# Revit family: TESK_Насос вертикальный_SVM(T)-120
name_source: partatom
category: Оборудование
units: mm (PartAtom-declared; Revit-internal decimal feet)

## family parameters
Всегда вертикально = Да
Классификация = Насос
На основе рабочей плоскости = Нет
Общий = Нет
При загрузке вырезать с полостями = Нет
Размер круглого соединителя = Использовать диаметр
Тип детали = Вставляется
Точка расчета площади = Нет

## types (38) — shared parameters
ADSK_Версия Revit = 2019
ADSK_Версия семейства = 1.0
ADSK_Диаметр условный = 125 мм
ADSK_Единица измерения = шт.
ADSK_Завод-изготовитель = TESK
ADSK_Классификация нагрузок = Прочее
ADSK_Количество = 1
ADSK_Количество фаз = 3
ADSK_Количество фаз числовое = 3
ADSK_Коэффициент мощности = 1
ADSK_Наименование краткое = Вертикальный многоступенчатый центробежный насос
ADSK_Напряжение = 400 В
URL = www.teskpump.ru
Материал_1 = TESK_Черный_Условный
Материал_2 = TESK_Нержавеющая сталь
Материал_КорпусДвигателя = TESK_Черный_Ребра_Условный
Таблица_Поиска = TESK_SVM(T)-120
УГО_Длина = 380 мм
Фланец_Толщина = 30 мм

## per-type parameters (varying)
| type | ADSK_Код изделия | ADSK_Масса | ADSK_Масса_Текст | ADSK_Наименование | ADSK_Номинальная мощность | ADSK_Полная мощность | D_Башня | Высота_Башня | Высота_Корпуса | Двигатель_Высота | Двигатель_ОтступКоробки | Двигатель_Ширина | Материал_КорпусУлитка | Напор максимальный | Толщина_ФланцаДвигателя |
| SVM 120-1 11kW 3x380V 50Hz IE3 | 77120-100003380NSSF | 230 | 230 | Вертикальный многоступенчатый центробежный насос SVM, DN125, PN25-40, Hmax=22м (3x380V 50Hz IE3) | 11 кВт | 11 кВ·А | 263 мм | 300 мм | 840 мм | 580 мм | 260 мм | 350 мм | TESK_Нержавеющая сталь | 22 | 17 мм |
| SVM 120-2-2 15kW 3x380V 50Hz IE3 | 77120-20-20003380NSSF | 245 | 245 | Вертикальный многоступенчатый центробежный насос SVM, DN125, PN25-40, Hmax=34м (3x380V 50Hz IE3) | 15 кВт | 15 кВ·А | 263 мм | 340 мм | 1000 мм | 580 мм | 260 мм | 350 мм | TESK_Нержавеющая сталь | 34 | 17 мм |
| SVM 120-2-1 18.5kW 3x380V 50Hz IE3 | 77120-20-10003380NSSF | 250 | 250 | Вертикальный многоступенчатый центробежный насос SVM, DN125, PN25-40, Hmax=41м (3x380V 50Hz IE3) | 19 кВт | 19 кВ·А | 263 мм | 340 мм | 1000 мм | 610 мм | 260 мм | 350 мм | TESK_Нержавеющая сталь | 41 | 18 мм |
| SVM 120-2 22kW 3x380V 50Hz IE3 | 77120-200003380NSSF | 285 | 285 | Вертикальный многоступенчатый центробежный насос SVM, DN125, PN25-40, Hmax=46м (3x380V 50Hz IE3) | 22 кВт | 22 кВ·А | 270 мм | 340 мм | 1000 мм | 645 мм | 285 мм | 360 мм | TESK_Нержавеющая сталь | 46 | 19 мм |
| SVM 120-3-2 30kW 3x380V 50Hz IE3 | 77120-30-20003380NSSF | 358 | 358 | Вертикальный многоступенчатый центробежный насос SVM, DN125, PN25-40, Hmax=57м (3x380V 50Hz IE3) | 30 кВт | 30 кВ·А | 300 мм | 380 мм | 1160 мм | 705 мм | 310 мм | 400 мм | TESK_Нержавеющая сталь | 57 | 21 мм |
| SVM 120-3-1 30kW 3x380V 50Hz IE3 | 77120-30-10003380NSSF | 360 | 360 | Вертикальный многоступенчатый центробежный насос SVM, DN125, PN25-40, Hmax=64м (3x380V 50Hz IE3) | 30 кВт | 30 кВ·А | 300 мм | 380 мм | 1160 мм | 705 мм | 310 мм | 400 мм | TESK_Нержавеющая сталь | 64 | 21 мм |
| SVM 120-3 30kW 3x380V 50Hz IE3 | 77120-300003380NSSF | 360 | 360 | Вертикальный многоступенчатый центробежный насос SVM, DN125, PN25-40, Hmax=69.5м (3x380V 50Hz IE3) | 30 кВт | 30 кВ·А | 300 мм | 380 мм | 1160 мм | 705 мм | 310 мм | 400 мм | TESK_Нержавеющая сталь | 69.5 | 21 мм |
| SVM 120-4-2 37kW 3x380V 50Hz IE3 | 77120-40-20003380NSSF | 400 | 400 | Вертикальный многоступенчатый центробежный насос SVM, DN125, PN25-40, Hmax=80.5м (3x380V 50Hz IE3) | 37 кВт | 37 кВ·А | 300 мм | 420 мм | 1320 мм | 705 мм | 310 мм | 400 мм | TESK_Нержавеющая сталь | 80.5 | 21 мм |
| SVM 120-4-1 37kW 3x380V 50Hz IE3 | 77120-40-10003380NSSF | 400 | 400 | Вертикальный многоступенчатый центробежный насос SVM, DN125, PN25-40, Hmax=87м (3x380V 50Hz IE3) | 37 кВт | 37 кВ·А | 300 мм | 420 мм | 1320 мм | 705 мм | 310 мм | 400 мм | TESK_Нержавеющая сталь | 87 | 21 мм |
| SVM 120-4 45kW 3x380V 50Hz IE3 | 77120-400003380NSSF | 460 | 460 | Вертикальный многоступенчатый центробежный насос SVM, DN125, PN25-40, Hmax=92.5м (3x380V 50Hz IE3) | 45 кВт | 45 кВ·А | 345 мм | 420 мм | 1320 мм | 740 мм | 340 мм | 460 мм | TESK_Нержавеющая сталь | 92.5 | 22 мм |
| SVM 120-5-2 45kW 3x380V 50Hz IE3 | 77120-50-20003380NSSF | 470 | 470 | Вертикальный многоступенчатый центробежный насос SVM, DN125, PN25-40, Hmax=104.5м (3x380V 50Hz IE3) | 45 кВт | 45 кВ·А | 345 мм | 480 мм | 1480 мм | 740 мм | 340 мм | 460 мм | TESK_Нержавеющая сталь | 104.5 | 22 мм |
| SVM 120-5-1 45kW 3x380V 50Hz IE3 | 77120-50-10003380NSSF | 470 | 470 | Вертикальный многоступенчатый центробежный насос SVM, DN125, PN25-40, Hmax=110.5м (3x380V 50Hz IE3) | 45 кВт | 45 кВ·А | 345 мм | 480 мм | 1480 мм | 740 мм | 340 мм | 460 мм | TESK_Нержавеющая сталь | 110.5 | 22 мм |
| SVM 120-5 55kW 3x380V 50Hz IE3 | 77120-500003380NSSF | 575 | 575 | Вертикальный многоступенчатый центробежный насос SVM, DN125, PN25-40, Hmax=115.5м (3x380V 50Hz IE3) | 55 кВт | 55 кВ·А | 413 мм | 500 мм | 1510 мм | 810 мм | 370 мм | 550 мм | TESK_Нержавеющая сталь | 115.5 | 24 мм |
| SVM 120-6-2 55kW 3x380V 50Hz IE3 | 77120-60-20003380NSSF | 585 | 585 | Вертикальный многоступенчатый центробежный насос SVM, DN125, PN25-40, Hmax=128м (3x380V 50Hz IE3) | 55 кВт | 55 кВ·А | 413 мм | 560 мм | 1670 мм | 810 мм | 370 мм | 550 мм | TESK_Нержавеющая сталь | 128 | 24 мм |
| SVM 120-6-1 55kW 3x380V 50Hz IE3 | 77120-60-10003380NSSF | 585 | 585 | Вертикальный многоступенчатый центробежный насос SVM, DN125, PN25-40, Hmax=134м (3x380V 50Hz IE3) | 55 кВт | 55 кВ·А | 413 мм | 560 мм | 1670 мм | 810 мм | 370 мм | 550 мм | TESK_Нержавеющая сталь | 134 | 24 мм |
| SVM 120-6 75kW 3x380V 50Hz IE3 | 77120-600003380NSSF | 705 | 705 | Вертикальный многоступенчатый центробежный насос SVM, DN125, PN25-40, Hmax=139м (3x380V 50Hz IE3) | 75 кВт | 75 кВ·А | 435 мм | 560 мм | 1670 мм | 870 мм | 410 мм | 580 мм | TESK_Нержавеющая сталь | 139 | 26 мм |
| SVM 120-7-2 75kW 3x380V 50Hz IE3 | 77120-70-20003380NSSF | 713 | 713 | Вертикальный многоступенчатый центробежный насос SVM, DN125, PN25-40, Hmax=151м (3x380V 50Hz IE3) | 75 кВт | 75 кВ·А | 435 мм | 600 мм | 1830 мм | 870 мм | 410 мм | 580 мм | TESK_Нержавеющая сталь | 151 | 26 мм |
| SVM 120-7-1 75kW 3x380V 50Hz IE3 | 77120-70-10003380NSSF | 715 | 715 | Вертикальный многоступенчатый центробежный насос SVM, DN125, PN25-40, Hmax=156.5м (3x380V 50Hz IE3) | 75 кВт | 75 кВ·А | 435 мм | 600 мм | 1830 мм | 870 мм | 410 мм | 580 мм | TESK_Нержавеющая сталь | 156.5 | 26 мм |
| SVM 120-7 75kW 3x380V 50Hz IE3 | 77120-700003380NSSF | 715 | 715 | Вертикальный многоступенчатый центробежный насос SVM, DN125, PN25-40, Hmax=162.5м (3x380V 50Hz IE3) | 75 кВт | 75 кВ·А | 435 мм | 600 мм | 1830 мм | 870 мм | 410 мм | 580 мм | TESK_Нержавеющая сталь | 162.5 | 26 мм |
| SVMT 120-1 11kW 3x380V 50Hz IE3 | 77120-100003380N | 230 | 230 | Вертикальный многоступенчатый центробежный насос SVMT, DN125, PN25-40, Hmax=22м (3x380V 50Hz IE3) | 11 кВт | 11 кВ·А | 263 мм | 300 мм | 840 мм | 580 мм | 260 мм | 350 мм | TESK_Черный_Условный | 22 | 17 мм |
| SVMT 120-2-2 15kW 3x380V 50Hz IE3 | 77120-20-20003380N | 245 | 245 | Вертикальный многоступенчатый центробежный насос SVMT, DN125, PN25-40, Hmax=34м (3x380V 50Hz IE3) | 15 кВт | 15 кВ·А | 263 мм | 340 мм | 1000 мм | 580 мм | 260 мм | 350 мм | TESK_Черный_Условный | 34 | 17 мм |
| SVMT 120-2-1 18.5kW 3x380V 50Hz IE3 | 77120-20-10003380N | 250 | 250 | Вертикальный многоступенчатый центробежный насос SVMT, DN125, PN25-40, Hmax=41м (3x380V 50Hz IE3) | 19 кВт | 19 кВ·А | 263 мм | 340 мм | 1000 мм | 610 мм | 260 мм | 350 мм | TESK_Черный_Условный | 41 | 18 мм |
| SVMT 120-2 22kW 3x380V 50Hz IE3 | 77120-200003380N | 285 | 285 | Вертикальный многоступенчатый центробежный насос SVMT, DN125, PN25-40, Hmax=46м (3x380V 50Hz IE3) | 22 кВт | 22 кВ·А | 270 мм | 340 мм | 1000 мм | 645 мм | 285 мм | 360 мм | TESK_Черный_Условный | 46 | 19 мм |
| SVMT 120-3-2 30kW 3x380V 50Hz IE3 | 77120-30-20003380N | 358 | 358 | Вертикальный многоступенчатый центробежный насос SVMT, DN125, PN25-40, Hmax=57м (3x380V 50Hz IE3) | 30 кВт | 30 кВ·А | 300 мм | 380 мм | 1160 мм | 705 мм | 310 мм | 400 мм | TESK_Черный_Условный | 57 | 21 мм |
| SVMT 120-3-1 30kW 3x380V 50Hz IE3 | 77120-30-10003380N | 360 | 360 | Вертикальный многоступенчатый центробежный насос SVMT, DN125, PN25-40, Hmax=64м (3x380V 50Hz IE3) | 30 кВт | 30 кВ·А | 300 мм | 380 мм | 1160 мм | 705 мм | 310 мм | 400 мм | TESK_Черный_Условный | 64 | 21 мм |
| SVMT 120-3 30kW 3x380V 50Hz IE3 | 77120-300003380N | 360 | 360 | Вертикальный многоступенчатый центробежный насос SVMT, DN125, PN25-40, Hmax=69.5м (3x380V 50Hz IE3) | 30 кВт | 30 кВ·А | 300 мм | 380 мм | 1160 мм | 705 мм | 310 мм | 400 мм | TESK_Черный_Условный | 69.5 | 21 мм |
| SVMT 120-4-2 37kW 3x380V 50Hz IE3 | 77120-40-20003380N | 400 | 400 | Вертикальный многоступенчатый центробежный насос SVMT, DN125, PN25-40, Hmax=80.5м (3x380V 50Hz IE3) | 37 кВт | 37 кВ·А | 300 мм | 420 мм | 1320 мм | 705 мм | 310 мм | 400 мм | TESK_Черный_Условный | 80.5 | 21 мм |
| SVMT 120-4-1 37kW 3x380V 50Hz IE3 | 77120-40-10003380N | 400 | 400 | Вертикальный многоступенчатый центробежный насос SVMT, DN125, PN25-40, Hmax=87м (3x380V 50Hz IE3) | 37 кВт | 37 кВ·А | 300 мм | 420 мм | 1320 мм | 705 мм | 310 мм | 400 мм | TESK_Черный_Условный | 87 | 21 мм |
| SVMT 120-4 45kW 3x380V 50Hz IE3 | 77120-400003380N | 460 | 460 | Вертикальный многоступенчатый центробежный насос SVMT, DN125, PN25-40, Hmax=92.5м (3x380V 50Hz IE3) | 45 кВт | 45 кВ·А | 345 мм | 420 мм | 1320 мм | 740 мм | 340 мм | 460 мм | TESK_Черный_Условный | 92.5 | 22 мм |
| SVMT 120-5-2 45kW 3x380V 50Hz IE3 | 77120-50-20003380N | 470 | 470 | Вертикальный многоступенчатый центробежный насос SVMT, DN125, PN25-40, Hmax=104.5м (3x380V 50Hz IE3) | 45 кВт | 45 кВ·А | 345 мм | 480 мм | 1480 мм | 740 мм | 340 мм | 460 мм | TESK_Черный_Условный | 104.5 | 22 мм |
| SVMT 120-5-1 45kW 3x380V 50Hz IE3 | 77120-50-10003380N | 470 | 470 | Вертикальный многоступенчатый центробежный насос SVMT, DN125, PN25-40, Hmax=110.5м (3x380V 50Hz IE3) | 45 кВт | 45 кВ·А | 345 мм | 480 мм | 1480 мм | 740 мм | 340 мм | 460 мм | TESK_Черный_Условный | 110.5 | 22 мм |
| SVMT 120-5 55kW 3x380V 50Hz IE3 | 77120-500003380N | 575 | 575 | Вертикальный многоступенчатый центробежный насос SVMT, DN125, PN25-40, Hmax=115.5м (3x380V 50Hz IE3) | 55 кВт | 55 кВ·А | 413 мм | 500 мм | 1510 мм | 810 мм | 370 мм | 550 мм | TESK_Черный_Условный | 115.5 | 24 мм |
| SVMT 120-6-2 55kW 3x380V 50Hz IE3 | 77120-60-20003380N | 585 | 585 | Вертикальный многоступенчатый центробежный насос SVMT, DN125, PN25-40, Hmax=128м (3x380V 50Hz IE3) | 55 кВт | 55 кВ·А | 413 мм | 560 мм | 1670 мм | 810 мм | 370 мм | 550 мм | TESK_Черный_Условный | 128 | 24 мм |
| SVMT 120-6-1 55kW 3x380V 50Hz IE3 | 77120-60-10003380N | 585 | 585 | Вертикальный многоступенчатый центробежный насос SVMT, DN125, PN25-40, Hmax=134м (3x380V 50Hz IE3) | 55 кВт | 55 кВ·А | 413 мм | 560 мм | 1670 мм | 810 мм | 370 мм | 550 мм | TESK_Черный_Условный | 134 | 24 мм |
| SVMT 120-6 75kW 3x380V 50Hz IE3 | 77120-600003380N | 705 | 705 | Вертикальный многоступенчатый центробежный насос SVMT, DN125, PN25-40, Hmax=139м (3x380V 50Hz IE3) | 75 кВт | 75 кВ·А | 435 мм | 560 мм | 1670 мм | 870 мм | 410 мм | 580 мм | TESK_Черный_Условный | 139 | 26 мм |
| SVMT 120-7-2 75kW 3x380V 50Hz IE3 | 77120-70-20003380N | 713 | 713 | Вертикальный многоступенчатый центробежный насос SVMT, DN125, PN25-40, Hmax=151м (3x380V 50Hz IE3) | 75 кВт | 75 кВ·А | 435 мм | 600 мм | 1830 мм | 870 мм | 410 мм | 580 мм | TESK_Черный_Условный | 151 | 26 мм |
| SVMT 120-7-1 75kW 3x380V 50Hz IE3 | 77120-70-10003380N | 715 | 715 | Вертикальный многоступенчатый центробежный насос SVMT, DN125, PN25-40, Hmax=156.5м (3x380V 50Hz IE3) | 75 кВт | 75 кВ·А | 435 мм | 600 мм | 1830 мм | 870 мм | 410 мм | 580 мм | TESK_Черный_Условный | 156.5 | 26 мм |
| SVMT 120-7 75kW 3x380V 50Hz IE3 | 77120-700003380N | 715 | 715 | Вертикальный многоступенчатый центробежный насос SVMT, DN125, PN25-40, Hmax=162.5м (3x380V 50Hz IE3) | 75 кВт | 75 кВ·А | 435 мм | 600 мм | 1830 мм | 870 мм | 410 мм | 580 мм | TESK_Черный_Условный | 162.5 | 26 мм |

note: column(s) folded — value = type name in every type: ADSK_Марка
